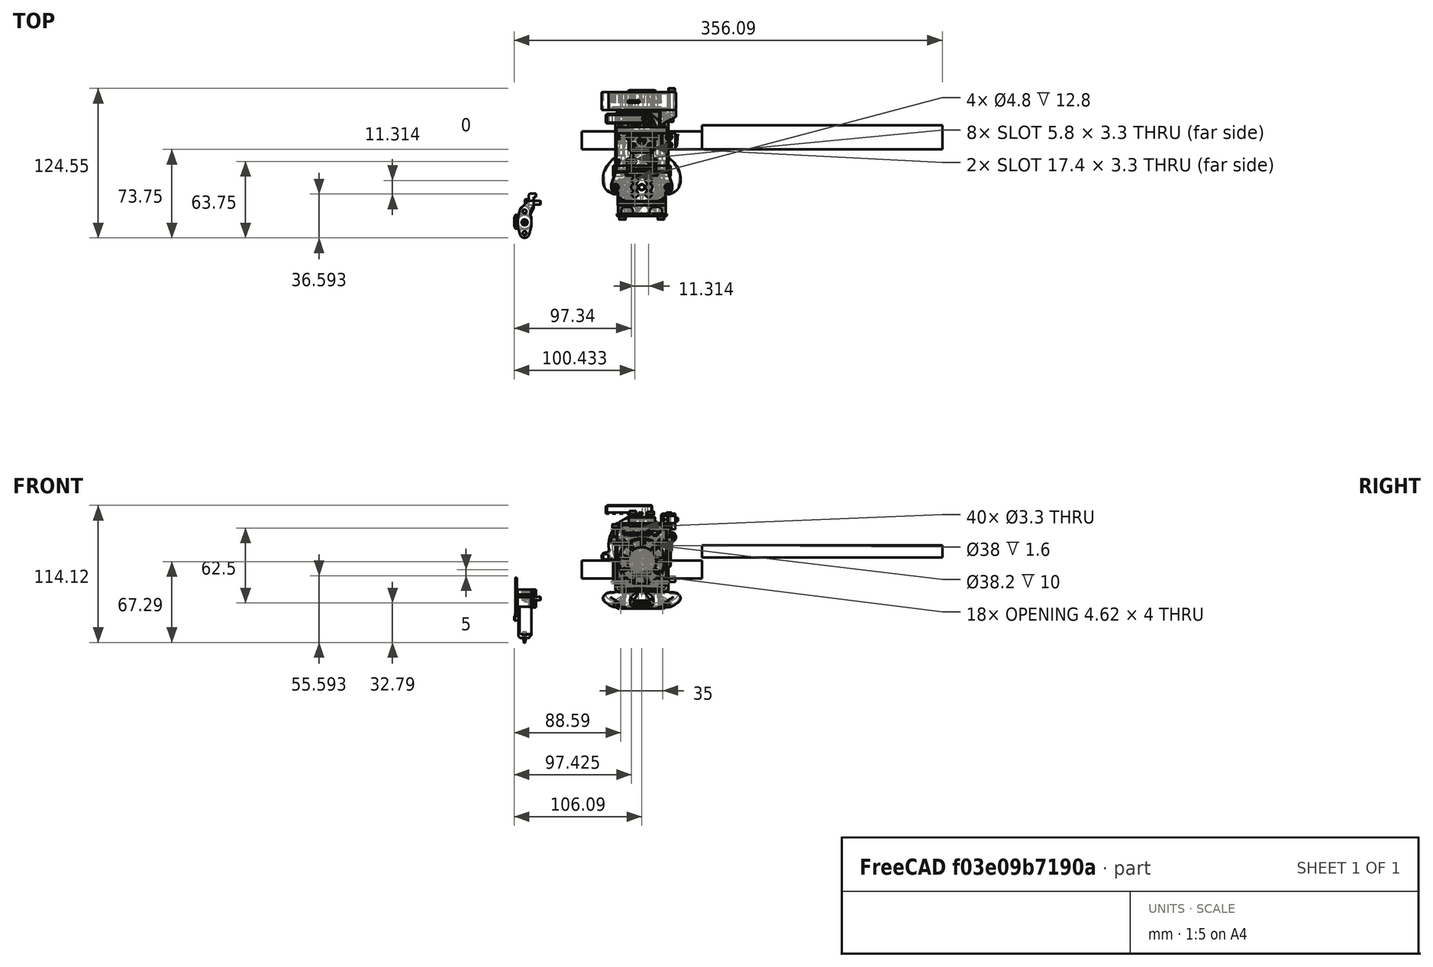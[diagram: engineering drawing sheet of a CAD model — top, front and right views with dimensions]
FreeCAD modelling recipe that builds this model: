
FCSTD DOCUMENT  (FreeCAD 0.19R24291 (Git))
Label: 2010-gantry
License: Other
LicenseURL: GPL3
objects: Part::Feature×106, Part::FeaturePython×104, App::Part×6, PartDesign::CoordinateSystem×2, Part::Box×2
note: 214 computed .brp shape members not serialized (recipe doc carries the construction recipe); baked Part::Feature solids carry a one-line shape summary decoded from their .brp

FEATURE [Part::FeaturePython] Screw1355  label="M3x40-Screw001"  # Fasteners workbench fastener (typed FeaturePython)
  Placement = pos=(-18.5,25.5,6) rot=(0,-1,0;1.5708rad)
  diameter = 4
  invert = false
  length = 10
  lengthCustom = 40
  matchOuter = true
  offset = 0
  thread = false
  type = 33
FEATURE [Part::FeaturePython] Screw1376  label="M2.5x12-Screw"  # Fasteners workbench fastener (typed FeaturePython)
  Placement = pos=(-6,-31.5,29.2) rot=(0,0,1;0rad)
  diameter = 3
  invert = false
  length = 10
  lengthCustom = 12
  matchOuter = true
  offset = 10
  thread = false
  type = 33
FEATURE [Part::Feature] Part__Feature112001140  label="adxl345 v009"
  shape: bbox 0.5 x 0.4946 x 0.1 mm, 6 faces (baked)
FEATURE [Part::FeaturePython] HeatSet014  label="M3x4-HeatSet010"  # WARN: FeaturePython — macro-defined, semantics opaque (R4)
  Placement = pos=(10.8,-13.5,27.705) rot=(-1,0,0;1.5708rad)
  diameter = 2
  invert = true
  offset = 0
FEATURE [Part::Feature] Part__Feature021  label="adxl345 v024"
  shape: bbox 0.5005 x 0.4962 x 0.1 mm, 6 faces (baked)
FEATURE [Part::Feature] Part__Feature013  label="adxl345 v016"
  shape: bbox 0.1939 x 0.3 x 0.1 mm, 6 faces (baked)
FEATURE [Part::Feature] Part__Feature112001127  label="adxl345 v017"
  shape: bbox 0.5 x 0.5 x 0.1 mm, 6 faces (baked)
FEATURE [Part::FeaturePython] Screw1381  label="M3x35-Screw"  # Fasteners workbench fastener (typed FeaturePython)
  Placement = pos=(17.0458,-16.5,41.0035) rot=(1,0,0;1.5708rad)
  diameter = 1
  invert = true
  length = 9
  lengthCustom = 35
  matchOuter = true
  offset = 0
  thread = false
  type = 39
FEATURE [Part::Feature] Part__Feature024  label="adxl345 v027"
  shape: bbox 0.5005 x 0.5054 x 0.15 mm, 6 faces (baked)
FEATURE [Part::FeaturePython] Nut  label="M3-Nut"  # Fasteners workbench fastener (typed FeaturePython)
  Placement = pos=(0,-15,-5.8) rot=(-1,0,0;1.5708rad)
  diameter = 4
  invert = true
  matchOuter = true
  offset = 0
  thread = false
  type = 7
FEATURE [Part::FeaturePython] Screw1371  label="M3x10-Screw189"  # Fasteners workbench fastener (typed FeaturePython)
  Placement = pos=(-94.0942,-44.3565,-16.7887) rot=(0,-1,0;1.5708rad)
  diameter = 4
  invert = false
  length = 10
  lengthCustom = 10
  matchOuter = true
  offset = 0
  thread = false
  type = 33
FEATURE [Part::FeaturePython] Screw020  label="M3x10-Screw"  # Fasteners workbench fastener (typed FeaturePython)
  Placement = pos=(-10.0042,-9.99647,39.1513) rot=(0,0,1;0rad)
  diameter = 4
  invert = false
  length = 10
  lengthCustom = 10
  matchOuter = true
  offset = 0
  thread = false
  type = 33
FEATURE [Part::FeaturePython] Nut005  label="M3-Nut030"  # Fasteners workbench fastener (typed FeaturePython)
  Placement = pos=(-13,15.5,-7) rot=(-1,0,0;1.5708rad)
  diameter = 4
  invert = false
  matchOuter = true
  offset = 0
  thread = false
  type = 7
FEATURE [Part::FeaturePython] HeatSet001  label="M3x4-HeatSet001"  # WARN: FeaturePython — macro-defined, semantics opaque (R4)
  Placement = pos=(-20,-36.5,11.7) rot=(0,-1,0;1.5708rad)
  baseObject = -> Chamfer005021077002006007019003029001 [Edge194]
  diameter = 2
  invert = false
  offset = 0
FEATURE [Part::FeaturePython] HeatSet019  label="M3x4-HeatSet017"  # WARN: FeaturePython — macro-defined, semantics opaque (R4)
  Placement = pos=(-21.9,-31.5,35) rot=(0,0,1;0rad)
  baseObject = -> Chamfer005021077002006007019003029001 [Edge1]
  diameter = 2
  invert = false
  offset = 0
FEATURE [Part::FeaturePython] Screw027  label="M3x25-Screw"  # Fasteners workbench fastener (typed FeaturePython)
  Placement = pos=(-10.8,-38.5,27.5) rot=(1,0,0;1.5708rad)
  diameter = 4
  invert = false
  length = 10
  lengthCustom = 25
  matchOuter = true
  offset = 0
  thread = false
  type = 33
FEATURE [Part::FeaturePython] HeatSet024  label="M3-HeatSet"  # WARN: FeaturePython — macro-defined, semantics opaque (R4)
  Placement = pos=(1.1e-14,13.5,42) rot=(-1,0,0;1.5708rad)
  baseObject = -> Chamfer005021077002006007019003032016001 [Edge74]
  diameter = 2
  invert = false
  offset = 0
FEATURE [Part::FeaturePython] Screw023  label="M3x12-Screw066"  # Fasteners workbench fastener (typed FeaturePython)
  Placement = pos=(21.9,-31.5,42) rot=(0,0,1;0rad)
  diameter = 4
  invert = false
  length = 10
  lengthCustom = 12
  matchOuter = true
  offset = 7
  thread = false
  type = 33
FEATURE [Part::FeaturePython] Screw1386  label="M3x12-Screw076"  # Fasteners workbench fastener (typed FeaturePython)
  Placement = pos=(0,25.5,42) rot=(-1,0,0;1.5708rad)
  baseObject = -> Chamfer001002006002 [Edge216]
  diameter = 4
  invert = true
  length = 4
  lengthCustom = 12
  matchOuter = true
  offset = 0
  thread = false
  type = 34
FEATURE [Part::FeaturePython] HeatSet006  label="M3x4-HeatSet007"  # WARN: FeaturePython — macro-defined, semantics opaque (R4)
  Placement = pos=(7.5,2.5,51) rot=(0,0,1;0rad)
  baseObject = -> Fusion036012039011002025018010027013001002002001002001029001 [Edge25]
  diameter = 2
  invert = false
  offset = 0
FEATURE [Part::Feature] Cut003  label="bl_touch_mount"
  Placement = pos=(-90,-44.75,-9.25) rot=(1,0,0;3.14159rad)
  shape: bbox 15.25 x 37 x 15 mm, 41 faces (baked)
FEATURE [Part::Feature] Part__Feature112001123  label="adxl345 v012"
  shape: bbox 0.5 x 0.5 x 0.1 mm, 6 faces (baked)
FEATURE [Part::FeaturePython] Screw1377  label="M2.5x12-Screw001"  # Fasteners workbench fastener (typed FeaturePython)
  Placement = pos=(6,-31.5,29.2) rot=(0,0,1;0rad)
  diameter = 3
  invert = false
  length = 10
  lengthCustom = 12
  matchOuter = true
  offset = 10
  thread = false
  type = 33
FEATURE [Part::FeaturePython] Screw018  label="M3x10-Screw186"  # Fasteners workbench fastener (typed FeaturePython)
  Placement = pos=(9.99577,-9.99647,39.1513) rot=(0,0,1;0rad)
  diameter = 4
  invert = true
  length = 10
  lengthCustom = 10
  matchOuter = true
  offset = 0
  thread = false
  type = 33
FEATURE [Part::Feature] Part__Feature020  label="adxl345 v023"
  shape: bbox 0.5 x 0.5 x 0.1 mm, 6 faces (baked)
FEATURE [Part::Feature] Part__Feature015  label="adxl345 v018"
  shape: bbox 0.5 x 0.5 x 0.1 mm, 6 faces (baked)
FEATURE [Part::Feature] Chamfer005021077002006007019003032007004003001001  label="1515-front-plate-r003"
  Placement = pos=(0,-13,10) rot=(1,0,0;1.5708rad)
  shape: bbox 48 x 9 x 57 mm, 252 faces (baked)
FEATURE [Part::FeaturePython] HeatSet015  label="M3x4-HeatSet012"  # WARN: FeaturePython — macro-defined, semantics opaque (R4)
  Placement = pos=(-10.8,-13.5,27.71) rot=(-1,0,0;1.5708rad)
  diameter = 2
  invert = true
  offset = 0
FEATURE [Part::Feature] Chamfer005021077002006007019003014001  label="face-plate"
  Placement = pos=(0,-56.5,-6) rot=(0,0,1;0rad)
  shape: bbox 41.5 x 7.5 x 53.5 mm, 789 faces (baked)
FEATURE [Part::FeaturePython] Screw1384  label="M3x12-Screw075"  # Fasteners workbench fastener (typed FeaturePython)
  Placement = pos=(17.5,18.5,-20.5) rot=(-1,0,0;1.5708rad)
  diameter = 4
  invert = false
  length = 4
  lengthCustom = 12
  matchOuter = true
  offset = 0
  thread = false
  type = 34
FEATURE [Part::Feature] Part__Feature112001136  label="5015 fan"
  Placement = pos=(-4.23967,32.8,25.9455) rot=(0.15487,0.698575,0.698575;3.44889rad)
  shape: bbox 61.97 x 15 x 62.93 mm, 220 faces (baked)
FEATURE [Part::FeaturePython] Screw1368  label="M3x25-Screw027"  # Fasteners workbench fastener (typed FeaturePython)
  Placement = pos=(24.8765,47.8,34.436) rot=(-1,0,0;1.5708rad)
  baseObject = -> Part__Feature112001136 [Edge8]
  diameter = 4
  invert = false
  length = 10
  lengthCustom = 25
  matchOuter = true
  offset = 0
  thread = false
  type = 33
FEATURE [Part::Feature] Part__Feature025  label="adxl345 v028"
  shape: bbox 0.5 x 0.5 x 0.15 mm, 6 faces (baked)
FEATURE [Part::Feature] Part__Feature112001130  label="adxl345 v034"
  shape: bbox 2 x 1 x 0.3 mm, 6 faces (baked)
FEATURE [Part::Feature] Part__Feature010  label="adxl345 v013"
  shape: bbox 0.5 x 0.4946 x 0.1 mm, 6 faces (baked)
FEATURE [Part::FeaturePython] Nut006  label="M3-Nut031"  # Fasteners workbench fastener (typed FeaturePython)
  Placement = pos=(24.8758,29.75,34.3023) rot=(1,0,0;1.5708rad)
  diameter = 4
  invert = false
  matchOuter = true
  offset = 0
  thread = false
  type = 7
FEATURE [Part::FeaturePython] Screw1385  label="M3x12-Screw074"  # Fasteners workbench fastener (typed FeaturePython)
  Placement = pos=(-17.5,18.5,-20.5) rot=(-1,0,0;1.5708rad)
  diameter = 4
  invert = true
  length = 4
  lengthCustom = 12
  matchOuter = true
  offset = 0
  thread = false
  type = 34
FEATURE [Part::Feature] Chamfer005021077002006007019003032007001  label="mosquito-mount-mod"
  Placement = pos=(0,-31.5,33) rot=(0,0,1;0rad)
  shape: bbox 51.01 x 27.77 x 40.81 mm, 154 faces (baked)
FEATURE [Part::FeaturePython] Screw1360  label="M3x35-Screw003"  # Fasteners workbench fastener (typed FeaturePython)
  Placement = pos=(12.9958,-16,-6.99647) rot=(1,0,0;1.5708rad)
  diameter = 4
  invert = true
  length = 10
  lengthCustom = 35
  matchOuter = true
  offset = 0
  thread = false
  type = 33
FEATURE [Part::FeaturePython] HeatSet017  label="M3x4-HeatSet013"  # WARN: FeaturePython — macro-defined, semantics opaque (R4)
  Placement = pos=(-10,25.5,19) rot=(0,-1,0;1.5708rad)
  baseObject = -> Chamfer005021077002006007019003032007003 [Edge5]
  diameter = 2
  invert = false
  offset = 0
FEATURE [Part::FeaturePython] Screw019  label="M3x10-Screw187"  # Fasteners workbench fastener (typed FeaturePython)
  Placement = pos=(-10.0042,10.0035,39.1513) rot=(0,0,1;0rad)
  diameter = 4
  invert = false
  length = 10
  lengthCustom = 10
  matchOuter = true
  offset = 0
  thread = false
  type = 33
FEATURE [Part::FeaturePython] HeatSet016  label="M3x4-HeatSet004"  # WARN: FeaturePython — macro-defined, semantics opaque (R4)
  Placement = pos=(10,25.5,6) rot=(0,1,0;1.5708rad)
  baseObject = -> Chamfer008009001 [Edge5]
  diameter = 2
  invert = false
  offset = 0
FEATURE [Part::Feature] Chamfer008009001  label="extruder-belt-tesioner"
  Placement = pos=(6,15,10) rot=(0,1,0;3.14159rad)
  shape: bbox 20 x 14.4 x 10 mm, 116 faces (baked)
FEATURE [Part::Feature] Part__Feature018  label="adxl345 v021"
  shape: bbox 0.5 x 2 x 0.1 mm, 6 faces (baked)
FEATURE [Part::FeaturePython] HeatSet018  label="M3x4-HeatSet018"  # WARN: FeaturePython — macro-defined, semantics opaque (R4)
  Placement = pos=(21.9,-31.5,35) rot=(0,0,1;0rad)
  baseObject = -> Chamfer005021077002006007019003029001 [Edge25]
  diameter = 2
  invert = false
  offset = 0
FEATURE [Part::Feature] Part__Feature028  label="adxl345 v031"
  shape: bbox 0.5 x 0.5054 x 0.15 mm, 6 faces (baked)
FEATURE [Part::Feature] Part__Feature005  label="adxl345 v008"
  shape: bbox 0.5 x 0.5 x 0.1 mm, 6 faces (baked)
FEATURE [Part::Feature] Fusion006002011004053036004001028003005014029  label="endstop-switch"
  Placement = pos=(28,7,46) rot=(0,0,1;1.5708rad)
  shape: bbox 12.18 x 13 x 6 mm, 43 faces (baked)
FEATURE [PartDesign::CoordinateSystem] LCS_toolhead_1515  label="LCS_toolhead-1515"
  AttacherType = Attacher::AttachEngine3D
FEATURE [Part::FeaturePython] Screw017  label="M3x10-Screw188"  # Fasteners workbench fastener (typed FeaturePython)
  Placement = pos=(9.99577,10.0035,39.1513) rot=(0,0,1;0rad)
  diameter = 4
  invert = true
  length = 10
  lengthCustom = 10
  matchOuter = true
  offset = 0
  thread = false
  type = 33
FEATURE [Part::Feature] Part__Feature112001141  label="adxl345 v011"
  shape: bbox 0.5 x 2 x 0.1 mm, 6 faces (baked)
FEATURE [Part::FeaturePython] Nut058  label="M3-Nut027"  # Fasteners workbench fastener (typed FeaturePython)
  Placement = pos=(17.05,15.5,41) rot=(-1,0,0;1.5708rad)
  diameter = 4
  invert = false
  matchOuter = true
  offset = 0
  thread = false
  type = 7
FEATURE [Part::Feature] Chamfer005021077002006007019003032007003  label="extruder-belt-tesioner001"
  Placement = pos=(-6,15,15) rot=(0,0,1;0rad)
  shape: bbox 20 x 14.4 x 10 mm, 116 faces (baked)
FEATURE [Part::Feature] Chamfer005021077002006007019003032016001  label="extruder-back-plate"
  Placement = pos=(1e-15,10,10) rot=(0,0.707107,0.707107;3.14159rad)
  shape: bbox 51.76 x 37.05 x 72.2 mm, 524 faces (baked)
FEATURE [Part::FeaturePython] Screw022  label="M3x12-Screw"  # Fasteners workbench fastener (typed FeaturePython)
  Placement = pos=(-21.9,-31.5,42) rot=(0,0,1;0rad)
  diameter = 4
  invert = false
  length = 10
  lengthCustom = 12
  matchOuter = true
  offset = 7
  thread = false
  type = 33
FEATURE [Part::Feature] Part__Feature029  label="adxl345 v032"
  shape: bbox 0.5 x 0.5054 x 0.15 mm, 6 faces (baked)
FEATURE [Part::Feature] Part__Feature026  label="adxl345 v029"
  shape: bbox 0.5 x 0.5054 x 0.15 mm, 6 faces (baked)
FEATURE [Part::Feature] Part__Feature011  label="adxl345 v014"
  shape: bbox 0.5 x 0.5 x 0.1 mm, 6 faces (baked)
FEATURE [Part::Feature] Part__Feature019  label="adxl345 v022"
  shape: bbox 0.5 x 0.4946 x 0.1 mm, 6 faces (baked)
FEATURE [Part::FeaturePython] Nut060  label="M3-Nut033"  # Fasteners workbench fastener (typed FeaturePython)
  Placement = pos=(17.5,8.59783,-20.5) rot=(1,0,0;1.5708rad)
  baseObject = -> Part__Feature003 [Edge202]
  diameter = 4
  invert = true
  matchOuter = true
  offset = 0
  thread = false
  type = 7
FEATURE [Part::FeaturePython] HeatSet004  label="M3x4-HeatSet009"  # WARN: FeaturePython — macro-defined, semantics opaque (R4)
  Placement = pos=(1e-14,7.5,46) rot=(0,0,1;0rad)
  baseObject = -> Body001002001 [Edge282]
  diameter = 2
  invert = true
  offset = 0
FEATURE [Part::FeaturePython] Screw1369  label="M3x25-Screw030"  # Fasteners workbench fastener (typed FeaturePython)
  Placement = pos=(10.8,-38.5,27.5) rot=(1,0,0;1.5708rad)
  diameter = 4
  invert = false
  length = 10
  lengthCustom = 25
  matchOuter = true
  offset = 0
  thread = false
  type = 33
FEATURE [Part::Feature] Part__Feature027  label="adxl345 v030"
  shape: bbox 0.5 x 0.5 x 0.15 mm, 6 faces (baked)
FEATURE [Part::Feature] Part__Feature112001139  label="BL-touch v3.x002"
  Placement = pos=(-97.5942,-60.3565,-13.2887) rot=(0,0,1;1.5708rad)
  shape: bbox 16.53 x 26.01 x 53.81 mm, 111 faces (baked)
FEATURE [App::Part] BL_Touch__1_001  label="BL-Touch <1>001"
  Group = -> [Part__Feature112001139,Screw1371,Cut003]
  Origin = -> Origin206
  Placement = pos=(70,8,28.5) rot=(0,0,1;0rad)
FEATURE [Part::FeaturePython] Screw1359  label="M3x35-Screw004"  # Fasteners workbench fastener (typed FeaturePython)
  Placement = pos=(-13.0042,-16,-6.99647) rot=(1,0,0;1.5708rad)
  diameter = 4
  invert = true
  length = 10
  lengthCustom = 35
  matchOuter = true
  offset = 0
  thread = false
  type = 33
FEATURE [Part::Feature] Part__Feature112001124  label="adxl345 v010"
  shape: bbox 0.5 x 0.5 x 0.1 mm, 6 faces (baked)
FEATURE [Part::Feature] Part__Feature112001143  label="dragon_support"
  Placement = pos=(-1.3e-14,-65.5,-44.5) rot=(1,0,0;3.14159rad)
  shape: bbox 40 x 20.25 x 9.266 mm, 50 faces (baked)
FEATURE [Part::FeaturePython] Screw1380  label="M3x35-Screw005"  # Fasteners workbench fastener (typed FeaturePython)
  Placement = pos=(-17.0542,-16.5,41.0035) rot=(1,0,0;1.5708rad)
  diameter = 1
  invert = true
  length = 9
  lengthCustom = 35
  matchOuter = true
  offset = 0
  thread = false
  type = 39
FEATURE [Part::Feature] Part__Feature112001133  label="mosquito_support"
  Placement = pos=(-2.78e-14,-21.6,27.5) rot=(0,0,1;0rad)
  shape: bbox 40 x 20.25 x 12 mm, 97 faces (baked)
FEATURE [Part::FeaturePython] Screw026  label="M3x8-Screw128"  # Fasteners workbench fastener (typed FeaturePython)
  Placement = pos=(3e-15,-20.15,-6) rot=(1,0,0;1.5708rad)
  baseObject = -> Part__Feature112001133 [Edge213]
  diameter = 4
  invert = true
  length = 10
  lengthCustom = 8
  matchOuter = true
  offset = 0
  thread = false
  type = 33
FEATURE [Part::Feature] Body001001001  label="endstop-cap"
  Placement = pos=(16,7,54) rot=(1,0,0;3.14159rad)
  shape: bbox 12 x 13 x 7.75 mm, 19 faces (baked)
FEATURE [Part::FeaturePython] Screw1383  label="M2x10-self-tapping"  # Fasteners workbench fastener (typed FeaturePython)
  Placement = pos=(22.75,10.25,53) rot=(0,0,1;0rad)
  baseObject = -> Body001001001 [Edge25]
  diameter = 2
  invert = false
  length = 5
  lengthCustom = 10
  matchOuter = true
  offset = 0
  thread = false
  type = 33
FEATURE [Part::FeaturePython] Screw1382  label="M2x10-self-tapping001"  # Fasteners workbench fastener (typed FeaturePython)
  Placement = pos=(22.75,3.75,53) rot=(0,0,1;0rad)
  baseObject = -> Body001001001 [Edge27]
  diameter = 2
  invert = false
  length = 5
  lengthCustom = 10
  matchOuter = true
  offset = 0
  thread = false
  type = 33
FEATURE [Part::FeaturePython] Screw1356  label="M3x40-Screw"  # Fasteners workbench fastener (typed FeaturePython)
  Placement = pos=(18.5,25.5,19) rot=(0,1,0;1.5708rad)
  diameter = 4
  invert = false
  length = 10
  lengthCustom = 40
  matchOuter = true
  offset = 0
  thread = false
  type = 33
FEATURE [Part::FeaturePython] HeatSet002  label="M3x4-HeatSet003"  # WARN: FeaturePython — macro-defined, semantics opaque (R4)
  Placement = pos=(20,-36.5,11.7) rot=(0,1,0;1.5708rad)
  baseObject = -> Chamfer005021077002006007019003029001 [Edge128]
  diameter = 2
  invert = true
  offset = 0
FEATURE [Part::Feature] Body001002001  label="top-plate-with-endstop"
  Placement = pos=(0,0,0) rot=(0,0,1;3.14159rad)
  shape: bbox 50.05 x 27 x 13 mm, 100 faces (baked)
FEATURE [Part::FeaturePython] Nut059  label="M3-Nut032"  # Fasteners workbench fastener (typed FeaturePython)
  Placement = pos=(-17.5,8.59783,-20.5) rot=(1,0,0;1.5708rad)
  baseObject = -> Part__Feature003 [Edge75]
  diameter = 4
  invert = false
  matchOuter = true
  offset = 0
  thread = false
  type = 7
FEATURE [Part::Feature] Fusion006002011004053036004001028003005014018035002010  label="mosquito-hotend"
  Placement = pos=(0,-31.5,-28) rot=(0,0,1;0rad)
  shape: bbox 27.01 x 18.86 x 47.01 mm, 355 faces, 0 solids (baked)
FEATURE [Part::FeaturePython] Nut004  label="M3-Nut009"  # Fasteners workbench fastener (typed FeaturePython)
  Placement = pos=(13,15.5,-7) rot=(-1,0,0;1.5708rad)
  diameter = 4
  invert = false
  matchOuter = true
  offset = 0
  thread = false
  type = 7
FEATURE [Part::Feature] Chamfer001002006002  label="extruder-cable-support"
  Placement = pos=(0,29.5,32) rot=(1,0,0;1.5708rad)
  shape: bbox 38.86 x 11.83 x 29.43 mm, 90 faces (baked)
FEATURE [Part::FeaturePython] HeatSet005  label="M3x4-HeatSet008"  # WARN: FeaturePython — macro-defined, semantics opaque (R4)
  Placement = pos=(-7.5,2.5,51) rot=(0,0,1;0rad)
  baseObject = -> Fusion036012039011002025018010027013001002002001002001029001 [Edge5]
  diameter = 2
  invert = false
  offset = 0
FEATURE [Part::Feature] Part__Feature006  label="extruderbottom-plate"
  Placement = pos=(0,17.6378,-29.79) rot=(1,0,0;1.5708rad)
  shape: bbox 44.1 x 27 x 22.2 mm, 66 faces (baked)
FEATURE [Part::Feature] Part__Feature004  label="adxl345 v007"
  shape: bbox 0.5 x 0.5 x 0.1 mm, 6 faces (baked)
FEATURE [Part::Feature] Part__Feature016  label="adxl345 v019"
  shape: bbox 0.5 x 0.5 x 0.1 mm, 6 faces (baked)
FEATURE [Part::FeaturePython] HeatSet003  label="M3x4-HeatSet"  # WARN: FeaturePython — macro-defined, semantics opaque (R4)
  Placement = pos=(20,-36.5,3.7) rot=(0,1,0;1.5708rad)
  baseObject = -> Chamfer005021077002006007019003029001 [Edge127]
  diameter = 2
  invert = true
  offset = 0
FEATURE [Part::Feature] Part__Feature112001126  label="adxl345 v005"
  shape: bbox 4 x 2 x 1 mm, 6 faces (baked)
FEATURE [Part::Feature] Part__Feature023  label="adxl345 v026"
  shape: bbox 0.1911 x 0.3 x 0.1 mm, 6 faces (baked)
FEATURE [Part::Feature] Chamfer005021077002006007019003029001  label="dragon-mount-mod"
  Placement = pos=(0,-31.5,33) rot=(0,0,1;0rad)
  shape: bbox 51.01 x 26.2 x 43.01 mm, 143 faces (baked)
FEATURE [Part::Feature] Part__Feature112001125  label="adxl345 v006"
  shape: bbox 0.2125 x 0.3 x 0.1 mm, 6 faces (baked)
FEATURE [Part::Feature] Part__Feature012  label="adxl345 v015"
  shape: bbox 0.2125 x 0.4 x 0.1 mm, 6 faces (baked)
FEATURE [Part::FeaturePython] Nut057  label="M3-Nut026"  # Fasteners workbench fastener (typed FeaturePython)
  Placement = pos=(-17.05,15.5,41) rot=(-1,0,0;1.5708rad)
  diameter = 4
  invert = false
  matchOuter = true
  offset = 0
  thread = false
  type = 7
FEATURE [Part::Feature] Part__Feature030  label="adxl345 v033"
  shape: bbox 0.5 x 0.5 x 0.15 mm, 6 faces (baked)
FEATURE [Part::Feature] Part__Feature112001131  label="4010-fan"
  Placement = pos=(-2.4e-14,-43.5,14) rot=(0,0,1;0rad)
  shape: bbox 40 x 10 x 40 mm, 104 faces (baked)
FEATURE [Part::FeaturePython] Screw1375  label="M3x25-Screw029"  # Fasteners workbench fastener (typed FeaturePython)
  Placement = pos=(16,-55.5,-2) rot=(1,0,0;1.5708rad)
  baseObject = -> Part__Feature112001131 [Edge121]
  diameter = 4
  invert = false
  length = 10
  lengthCustom = 25
  matchOuter = true
  offset = 2
  thread = false
  type = 33
FEATURE [Part::FeaturePython] Screw1374  label="M3x25-Screw004"  # Fasteners workbench fastener (typed FeaturePython)
  Placement = pos=(-16,-55.5,-2) rot=(1,0,0;1.5708rad)
  baseObject = -> Part__Feature112001131 [Edge127]
  diameter = 4
  invert = false
  length = 10
  lengthCustom = 25
  matchOuter = true
  offset = 2
  thread = false
  type = 33
FEATURE [Part::FeaturePython] Screw1372  label="M3x20-Screw023"  # Fasteners workbench fastener (typed FeaturePython)
  Placement = pos=(-16,-55.5,30) rot=(1,0,0;1.5708rad)
  baseObject = -> Part__Feature112001131 [Edge130]
  diameter = 4
  invert = false
  length = 10
  lengthCustom = 20
  matchOuter = true
  offset = 2
  thread = false
  type = 33
FEATURE [Part::FeaturePython] Screw1373  label="M3x20-Screw024"  # Fasteners workbench fastener (typed FeaturePython)
  Placement = pos=(16,-55.5,30) rot=(1,0,0;1.5708rad)
  baseObject = -> Part__Feature112001131 [Edge124]
  diameter = 4
  invert = false
  length = 10
  lengthCustom = 20
  matchOuter = true
  offset = 2
  thread = false
  type = 33
FEATURE [Part::Feature] Part__Feature017  label="adxl345 v020"
  shape: bbox 0.5 x 0.5 x 0.1 mm, 6 faces (baked)
FEATURE [Part::Feature] Part__Feature022  label="adxl345 v025"
  shape: bbox 0.1911 x 0.4 x 0.1 mm, 6 faces (baked)
FEATURE [Part::Feature] Part__Feature003  label="duct-tri-horn"
  Placement = pos=(0,10.5978,-18) rot=(1,0,0;1.5708rad)
  shape: bbox 65.34 x 50.74 x 15.61 mm, 106 faces (baked)
FEATURE [Part::FeaturePython] Screw  label="M3x8-Screw"  # Fasteners workbench fastener (typed FeaturePython)
  Placement = pos=(0,7.5,48.5) rot=(0,0,1;0rad)
  diameter = 1
  invert = false
  length = 1
  lengthCustom = 8
  matchOuter = true
  offset = 0
  thread = false
  type = 39
FEATURE [Part::Feature] Fusion036012039011002025018010027013001002002001002001029001  label="adxl-mount"
  Placement = pos=(0,-31.5,33) rot=(0,0,1;0rad)
  shape: bbox 22 x 12.5 x 6.5 mm, 26 faces (baked)
FEATURE [Part::FeaturePython] Screw1378  label="M3x6-Screw"  # Fasteners workbench fastener (typed FeaturePython)
  Placement = pos=(-7.5,2.5,53) rot=(0,0,1;0rad)
  baseObject = -> Fusion036012039011002025018010027013001002002001002001029001 [Edge2]
  diameter = 4
  invert = false
  length = 1
  lengthCustom = 6
  matchOuter = true
  offset = 2.4
  thread = false
  type = 33
FEATURE [Part::FeaturePython] Screw1379  label="M3x6-Screw105"  # Fasteners workbench fastener (typed FeaturePython)
  Placement = pos=(7.5,2.5,52.6) rot=(0,0,1;0rad)
  baseObject = -> Fusion036012039011002025018010027013001002002001002001029001 [Edge47]
  diameter = 4
  invert = false
  length = 1
  lengthCustom = 6
  matchOuter = true
  offset = 2
  thread = false
  type = 33
FEATURE [Part::Feature] Part__Feature112001129  label="adxl345 v3"
  shape: bbox 6 x 3 x 0.5 mm, 6 faces (baked)
FEATURE [Part::Feature] Part__Feature112001128  label="adxl345 v004"
  shape: bbox 20 x 15 x 1.27 mm, 8 faces (baked)
FEATURE [App::Part] adxl345_v3  label="adxl345"
  Group = -> [Part__Feature112001129,Part__Feature112001128,Part__Feature112001126,Part__Feature112001125,Part__Feature004,Part__Feature005,Part__Feature112001140,Part__Feature112001124,Part__Feature112001141,Part__Feature112001123,Part__Feature010,Part__Feature011,Part__Feature012,Part__Feature013,Part__Feature112001127,Part__Feature015,Part__Feature016,Part__Feature017,Part__Feature018,Part__Feature019,+12 more]
  Origin = -> Origin004
  Placement = pos=(-10,0.5,52.5) rot=(0,0,1;0rad)
FEATURE [App::Part] Part197  label="toolhead-carrier-sherpa-1515"
  Group = -> [Fusion006002011004053036004001028003005014018035002010,Part__Feature112001133,Part__Feature112001136,Part__Feature112001131,BL_Touch__1_001,Nut006,Nut058,Nut005,Nut004,Screw1355,Screw1356,Nut057,Screw1360,Screw1359,Screw1368,Screw022,Screw018,Screw020,Screw023,Screw019,Screw017,Screw026,Screw1376,Screw1377,Screw1369,Screw027,Screw1373,Screw1375,Screw1374,Screw1372,adxl345_v3,+42 more]
  Origin = -> Origin205
  Placement = pos=(0,7.5,-5) rot=(0,0,1;0rad)
FEATURE [Part::Box] Box  label="Cube"
  AttacherType = Attacher::AttachEngine3D
  Height = 15
  Length = 100
  Placement = pos=(-50,0,0) rot=(0,0,1;0rad)
  Width = 15
FEATURE [Part::Box] Box001  label="Cube001"
  AttacherType = Attacher::AttachEngine3D
  Height = 10
  Length = 200
  Placement = pos=(50,0,17.5) rot=(0,0,1;0rad)
  Width = 20
FEATURE [Part::FeaturePython] Screw1387  label="M3x40-Screw002"  # Fasteners workbench fastener (typed FeaturePython)
  Placement = pos=(-18.5,25.5,6) rot=(0,-1,0;1.5708rad)
  diameter = 4
  invert = false
  length = 10
  lengthCustom = 40
  matchOuter = true
  offset = 0
  thread = false
  type = 33
FEATURE [Part::Feature] Part__Feature112001144  label="adxl345 v035"
  shape: bbox 0.5 x 2 x 0.1 mm, 6 faces (baked)
FEATURE [Part::FeaturePython] Screw1388  label="M2.5x12-Screw002"  # Fasteners workbench fastener (typed FeaturePython)
  Placement = pos=(-6,-31.5,29.2) rot=(0,0,1;0rad)
  diameter = 3
  invert = false
  length = 10
  lengthCustom = 12
  matchOuter = true
  offset = 10
  thread = false
  type = 33
FEATURE [Part::Feature] Part__Feature112001145  label="adxl345 v036"
  shape: bbox 0.5 x 0.4946 x 0.1 mm, 6 faces (baked)
FEATURE [Part::FeaturePython] HeatSet025  label="M3x4-HeatSet019"  # WARN: FeaturePython — macro-defined, semantics opaque (R4)
  Placement = pos=(10.8,-13.5,27.705) rot=(-1,0,0;1.5708rad)
  diameter = 2
  invert = true
  offset = 0
FEATURE [Part::Feature] Part__Feature112001146  label="adxl345 v037"
  shape: bbox 0.5005 x 0.4962 x 0.1 mm, 6 faces (baked)
FEATURE [Part::Feature] Part__Feature112001147  label="adxl345 v038"
  shape: bbox 0.1939 x 0.3 x 0.1 mm, 6 faces (baked)
FEATURE [Part::Feature] Part__Feature112001148  label="adxl345 v039"
  shape: bbox 0.5 x 0.5 x 0.1 mm, 6 faces (baked)
FEATURE [Part::FeaturePython] Screw1393  label="M3x35-Screw006"  # Fasteners workbench fastener (typed FeaturePython)
  Placement = pos=(17.0458,-16.5,41.0035) rot=(1,0,0;1.5708rad)
  diameter = 1
  invert = true
  length = 9
  lengthCustom = 35
  matchOuter = true
  offset = 0
  thread = false
  type = 39
FEATURE [Part::Feature] Part__Feature112001149  label="adxl345 v040"
  shape: bbox 0.5005 x 0.5054 x 0.15 mm, 6 faces (baked)
FEATURE [Part::FeaturePython] Nut061  label="M3-Nut034"  # Fasteners workbench fastener (typed FeaturePython)
  Placement = pos=(0,-15,-5.8) rot=(-1,0,0;1.5708rad)
  diameter = 4
  invert = true
  matchOuter = true
  offset = 0
  thread = false
  type = 7
FEATURE [Part::FeaturePython] Screw1394  label="M3x10-Screw190"  # Fasteners workbench fastener (typed FeaturePython)
  Placement = pos=(-94.0942,-44.3565,-16.7887) rot=(0,-1,0;1.5708rad)
  diameter = 4
  invert = false
  length = 10
  lengthCustom = 10
  matchOuter = true
  offset = 0
  thread = false
  type = 33
FEATURE [Part::FeaturePython] Screw1395  label="M3x10-Screw191"  # Fasteners workbench fastener (typed FeaturePython)
  Placement = pos=(-10.0042,-9.99647,39.1513) rot=(0,0,1;0rad)
  diameter = 4
  invert = false
  length = 10
  lengthCustom = 10
  matchOuter = true
  offset = 0
  thread = false
  type = 33
FEATURE [Part::FeaturePython] Nut062  label="M3-Nut035"  # Fasteners workbench fastener (typed FeaturePython)
  Placement = pos=(-13,15.5,-7) rot=(-1,0,0;1.5708rad)
  diameter = 4
  invert = false
  matchOuter = true
  offset = 0
  thread = false
  type = 7
FEATURE [Part::FeaturePython] HeatSet026  label="M3x4-HeatSet020"  # WARN: FeaturePython — macro-defined, semantics opaque (R4)
  Placement = pos=(-20,-36.5,11.7) rot=(0,-1,0;1.5708rad)
  baseObject = -> Chamfer005021077002006007019003032007004003001009 [Edge194]
  diameter = 2
  invert = false
  offset = 0
FEATURE [Part::FeaturePython] HeatSet027  label="M3x4-HeatSet021"  # WARN: FeaturePython — macro-defined, semantics opaque (R4)
  Placement = pos=(-21.9,-31.5,35) rot=(0,0,1;0rad)
  baseObject = -> Chamfer005021077002006007019003032007004003001009 [Edge1]
  diameter = 2
  invert = false
  offset = 0
FEATURE [Part::FeaturePython] Screw1396  label="M3x25-Screw033"  # Fasteners workbench fastener (typed FeaturePython)
  Placement = pos=(-10.8,-38.5,27.5) rot=(1,0,0;1.5708rad)
  diameter = 4
  invert = false
  length = 10
  lengthCustom = 25
  matchOuter = true
  offset = 0
  thread = false
  type = 33
FEATURE [Part::FeaturePython] HeatSet028  label="M3-HeatSet001"  # WARN: FeaturePython — macro-defined, semantics opaque (R4)
  Placement = pos=(1.1e-14,13.5,42) rot=(-1,0,0;1.5708rad)
  baseObject = -> Chamfer005021077002006007019003032007004003001007 [Edge74]
  diameter = 2
  invert = false
  offset = 0
FEATURE [Part::FeaturePython] Screw1397  label="M3x12-Screw077"  # Fasteners workbench fastener (typed FeaturePython)
  Placement = pos=(21.9,-31.5,42) rot=(0,0,1;0rad)
  diameter = 4
  invert = false
  length = 10
  lengthCustom = 12
  matchOuter = true
  offset = 7
  thread = false
  type = 33
FEATURE [Part::FeaturePython] Screw1399  label="M3x12-Screw078"  # Fasteners workbench fastener (typed FeaturePython)
  Placement = pos=(0,25.5,42) rot=(-1,0,0;1.5708rad)
  baseObject = -> Chamfer005021077002006007019003032007004003001008 [Edge216]
  diameter = 4
  invert = true
  length = 4
  lengthCustom = 12
  matchOuter = true
  offset = 0
  thread = false
  type = 34
FEATURE [Part::FeaturePython] HeatSet029  label="M3x4-HeatSet022"  # WARN: FeaturePython — macro-defined, semantics opaque (R4)
  Placement = pos=(7.5,2.5,51) rot=(0,0,1;0rad)
  baseObject = -> Fusion036012039011002025018010027013001002002001002001029004 [Edge25]
  diameter = 2
  invert = false
  offset = 0
FEATURE [Part::Feature] Cut004  label="bl_touch_mount001"
  Placement = pos=(-90,-44.75,-9.25) rot=(1,0,0;3.14159rad)
  shape: bbox 15.25 x 37 x 15 mm, 41 faces (baked)
FEATURE [Part::Feature] Part__Feature112001150  label="adxl345 v041"
  shape: bbox 0.5 x 0.5 x 0.1 mm, 6 faces (baked)
FEATURE [Part::FeaturePython] Screw1400  label="M2.5x12-Screw003"  # Fasteners workbench fastener (typed FeaturePython)
  Placement = pos=(6,-31.5,29.2) rot=(0,0,1;0rad)
  diameter = 3
  invert = false
  length = 10
  lengthCustom = 12
  matchOuter = true
  offset = 10
  thread = false
  type = 33
FEATURE [Part::FeaturePython] Screw1401  label="M3x10-Screw192"  # Fasteners workbench fastener (typed FeaturePython)
  Placement = pos=(9.99577,-9.99647,39.1513) rot=(0,0,1;0rad)
  diameter = 4
  invert = true
  length = 10
  lengthCustom = 10
  matchOuter = true
  offset = 0
  thread = false
  type = 33
FEATURE [Part::Feature] Part__Feature112001151  label="adxl345 v042"
  shape: bbox 0.5 x 0.5 x 0.1 mm, 6 faces (baked)
FEATURE [Part::Feature] Part__Feature112001152  label="adxl345 v043"
  shape: bbox 0.5 x 0.5 x 0.1 mm, 6 faces (baked)
FEATURE [Part::Feature] Chamfer005021077002006007019003032007004003001002  label="1515-front-plate-r004"
  Placement = pos=(0,-13,10) rot=(1,0,0;1.5708rad)
  shape: bbox 48 x 9 x 57 mm, 252 faces (baked)
FEATURE [Part::FeaturePython] HeatSet030  label="M3x4-HeatSet023"  # WARN: FeaturePython — macro-defined, semantics opaque (R4)
  Placement = pos=(-10.8,-13.5,27.71) rot=(-1,0,0;1.5708rad)
  diameter = 2
  invert = true
  offset = 0
FEATURE [Part::Feature] Chamfer005021077002006007019003032007004003001003  label="face-plate001"
  Placement = pos=(0,-56.5,-6) rot=(0,0,1;0rad)
  shape: bbox 41.5 x 7.5 x 53.5 mm, 789 faces (baked)
FEATURE [Part::FeaturePython] Screw1402  label="M3x12-Screw079"  # Fasteners workbench fastener (typed FeaturePython)
  Placement = pos=(17.5,18.5,-20.5) rot=(-1,0,0;1.5708rad)
  diameter = 4
  invert = false
  length = 4
  lengthCustom = 12
  matchOuter = true
  offset = 0
  thread = false
  type = 34
FEATURE [Part::Feature] Part__Feature112001153  label="5015 fan001"
  Placement = pos=(-4.23967,32.8,25.9455) rot=(0.15487,0.698575,0.698575;3.44889rad)
  shape: bbox 61.97 x 15 x 62.93 mm, 220 faces (baked)
FEATURE [Part::FeaturePython] Screw1398  label="M3x25-Screw034"  # Fasteners workbench fastener (typed FeaturePython)
  Placement = pos=(24.8765,47.8,34.436) rot=(-1,0,0;1.5708rad)
  baseObject = -> Part__Feature112001153 [Edge8]
  diameter = 4
  invert = false
  length = 10
  lengthCustom = 25
  matchOuter = true
  offset = 0
  thread = false
  type = 33
FEATURE [Part::Feature] Part__Feature112001154  label="adxl345 v044"
  shape: bbox 0.5 x 0.5 x 0.15 mm, 6 faces (baked)
FEATURE [Part::Feature] Part__Feature112001155  label="adxl345 v045"
  shape: bbox 2 x 1 x 0.3 mm, 6 faces (baked)
FEATURE [Part::Feature] Part__Feature112001156  label="adxl345 v046"
  shape: bbox 0.5 x 0.4946 x 0.1 mm, 6 faces (baked)
FEATURE [Part::FeaturePython] Nut063  label="M3-Nut036"  # Fasteners workbench fastener (typed FeaturePython)
  Placement = pos=(24.8758,29.75,34.3023) rot=(1,0,0;1.5708rad)
  diameter = 4
  invert = false
  matchOuter = true
  offset = 0
  thread = false
  type = 7
FEATURE [Part::FeaturePython] Screw1403  label="M3x12-Screw080"  # Fasteners workbench fastener (typed FeaturePython)
  Placement = pos=(-17.5,18.5,-20.5) rot=(-1,0,0;1.5708rad)
  diameter = 4
  invert = true
  length = 4
  lengthCustom = 12
  matchOuter = true
  offset = 0
  thread = false
  type = 34
FEATURE [Part::Feature] Chamfer005021077002006007019003032007004003001004  label="mosquito-mount-mod001"
  Placement = pos=(0,-31.5,33) rot=(0,0,1;0rad)
  shape: bbox 51.01 x 27.77 x 40.81 mm, 154 faces (baked)
FEATURE [Part::FeaturePython] Screw1404  label="M3x35-Screw007"  # Fasteners workbench fastener (typed FeaturePython)
  Placement = pos=(12.9958,-16,-6.99647) rot=(1,0,0;1.5708rad)
  diameter = 4
  invert = true
  length = 10
  lengthCustom = 35
  matchOuter = true
  offset = 0
  thread = false
  type = 33
FEATURE [Part::FeaturePython] HeatSet031  label="M3x4-HeatSet024"  # WARN: FeaturePython — macro-defined, semantics opaque (R4)
  Placement = pos=(-10,25.5,19) rot=(0,-1,0;1.5708rad)
  baseObject = -> Chamfer005021077002006007019003032007004003001006 [Edge5]
  diameter = 2
  invert = false
  offset = 0
FEATURE [Part::FeaturePython] Screw1406  label="M3x10-Screw193"  # Fasteners workbench fastener (typed FeaturePython)
  Placement = pos=(-10.0042,10.0035,39.1513) rot=(0,0,1;0rad)
  diameter = 4
  invert = false
  length = 10
  lengthCustom = 10
  matchOuter = true
  offset = 0
  thread = false
  type = 33
FEATURE [Part::FeaturePython] HeatSet032  label="M3x4-HeatSet025"  # WARN: FeaturePython — macro-defined, semantics opaque (R4)
  Placement = pos=(10,25.5,6) rot=(0,1,0;1.5708rad)
  baseObject = -> Chamfer005021077002006007019003032007004003001005 [Edge5]
  diameter = 2
  invert = false
  offset = 0
FEATURE [Part::Feature] Chamfer005021077002006007019003032007004003001005  label="extruder-belt-tesioner002"
  Placement = pos=(6,15,10) rot=(0,1,0;3.14159rad)
  shape: bbox 20 x 14.4 x 10 mm, 116 faces (baked)
FEATURE [Part::Feature] Part__Feature112001157  label="adxl345 v047"
  shape: bbox 0.5 x 2 x 0.1 mm, 6 faces (baked)
FEATURE [Part::FeaturePython] HeatSet033  label="M3x4-HeatSet026"  # WARN: FeaturePython — macro-defined, semantics opaque (R4)
  Placement = pos=(21.9,-31.5,35) rot=(0,0,1;0rad)
  baseObject = -> Chamfer005021077002006007019003032007004003001009 [Edge25]
  diameter = 2
  invert = false
  offset = 0
FEATURE [Part::Feature] Part__Feature112001158  label="adxl345 v048"
  shape: bbox 0.5 x 0.5054 x 0.15 mm, 6 faces (baked)
FEATURE [Part::Feature] Part__Feature112001159  label="adxl345 v049"
  shape: bbox 0.5 x 0.5 x 0.1 mm, 6 faces (baked)
FEATURE [Part::Feature] Part__Feature112001160  label="adxl345 v050"
  shape: bbox 20 x 15 x 1.27 mm, 8 faces (baked)
FEATURE [Part::Feature] Fusion036012039011002025018010027013001002002001002001029002  label="endstop-switch001"
  Placement = pos=(28,7,46) rot=(0,0,1;1.5708rad)
  shape: bbox 12.18 x 13 x 6 mm, 43 faces (baked)
FEATURE [PartDesign::CoordinateSystem] LCS_toolhead_1516  label="LCS_toolhead-1516"
  AttacherType = Attacher::AttachEngine3D
FEATURE [Part::FeaturePython] Screw1408  label="M3x10-Screw194"  # Fasteners workbench fastener (typed FeaturePython)
  Placement = pos=(9.99577,10.0035,39.1513) rot=(0,0,1;0rad)
  diameter = 4
  invert = true
  length = 10
  lengthCustom = 10
  matchOuter = true
  offset = 0
  thread = false
  type = 33
FEATURE [Part::FeaturePython] Nut064  label="M3-Nut037"  # Fasteners workbench fastener (typed FeaturePython)
  Placement = pos=(17.05,15.5,41) rot=(-1,0,0;1.5708rad)
  diameter = 4
  invert = false
  matchOuter = true
  offset = 0
  thread = false
  type = 7
FEATURE [Part::Feature] Chamfer005021077002006007019003032007004003001006  label="extruder-belt-tesioner003"
  Placement = pos=(-6,15,15) rot=(0,0,1;0rad)
  shape: bbox 20 x 14.4 x 10 mm, 116 faces (baked)
FEATURE [Part::Feature] Chamfer005021077002006007019003032007004003001007  label="extruder-back-plate001"
  Placement = pos=(1e-15,10,10) rot=(0,0.707107,0.707107;3.14159rad)
  shape: bbox 51.76 x 37.05 x 72.2 mm, 524 faces (baked)
FEATURE [Part::FeaturePython] Screw1409  label="M3x12-Screw081"  # Fasteners workbench fastener (typed FeaturePython)
  Placement = pos=(-21.9,-31.5,42) rot=(0,0,1;0rad)
  diameter = 4
  invert = false
  length = 10
  lengthCustom = 12
  matchOuter = true
  offset = 7
  thread = false
  type = 33
FEATURE [Part::Feature] Part__Feature112001161  label="adxl345 v051"
  shape: bbox 0.5 x 0.5054 x 0.15 mm, 6 faces (baked)
FEATURE [Part::Feature] Part__Feature112001162  label="adxl345 v052"
  shape: bbox 0.5 x 0.5054 x 0.15 mm, 6 faces (baked)
FEATURE [Part::Feature] Part__Feature112001163  label="adxl345 v053"
  shape: bbox 0.5 x 0.5 x 0.1 mm, 6 faces (baked)
FEATURE [Part::Feature] Part__Feature112001164  label="adxl345 v054"
  shape: bbox 0.5 x 0.4946 x 0.1 mm, 6 faces (baked)
FEATURE [Part::FeaturePython] Nut065  label="M3-Nut038"  # Fasteners workbench fastener (typed FeaturePython)
  Placement = pos=(17.5,8.59783,-20.5) rot=(1,0,0;1.5708rad)
  baseObject = -> Part__Feature112001181 [Edge202]
  diameter = 4
  invert = true
  matchOuter = true
  offset = 0
  thread = false
  type = 7
FEATURE [Part::FeaturePython] HeatSet034  label="M3x4-HeatSet027"  # WARN: FeaturePython — macro-defined, semantics opaque (R4)
  Placement = pos=(1.03e-14,7.5,2) rot=(0,0,1;0rad)
  baseObject = -> Body001002003 [Edge282]
  diameter = 2
  invert = true
  offset = 0
FEATURE [Part::FeaturePython] Screw1411  label="M3x25-Screw035"  # Fasteners workbench fastener (typed FeaturePython)
  Placement = pos=(10.8,-38.5,27.5) rot=(1,0,0;1.5708rad)
  diameter = 4
  invert = false
  length = 10
  lengthCustom = 25
  matchOuter = true
  offset = 0
  thread = false
  type = 33
FEATURE [Part::Feature] Part__Feature112001165  label="adxl345 v055"
  shape: bbox 0.5 x 0.5 x 0.15 mm, 6 faces (baked)
FEATURE [Part::Feature] Part__Feature112001166  label="BL-touch v3.x003"
  Placement = pos=(-97.5942,-60.3565,-13.2887) rot=(0,0,1;1.5708rad)
  shape: bbox 16.53 x 26.01 x 53.81 mm, 111 faces (baked)
FEATURE [App::Part] BL_Touch__1_002  label="BL-Touch <1>002"
  Group = -> [Part__Feature112001166,Screw1394,Cut004]
  Origin = -> Origin208
  Placement = pos=(70,8,28.5) rot=(0,0,1;0rad)
FEATURE [Part::FeaturePython] Screw1412  label="M3x35-Screw008"  # Fasteners workbench fastener (typed FeaturePython)
  Placement = pos=(-13.0042,-16,-6.99647) rot=(1,0,0;1.5708rad)
  diameter = 4
  invert = true
  length = 10
  lengthCustom = 35
  matchOuter = true
  offset = 0
  thread = false
  type = 33
FEATURE [Part::Feature] Part__Feature112001167  label="adxl345 v056"
  shape: bbox 0.5 x 0.5 x 0.1 mm, 6 faces (baked)
FEATURE [Part::Feature] Part__Feature112001168  label="dragon_support001"
  Placement = pos=(-1.3e-14,-65.5,-44.5) rot=(1,0,0;3.14159rad)
  shape: bbox 40 x 20.25 x 9.266 mm, 50 faces (baked)
FEATURE [Part::FeaturePython] Screw1413  label="M3x35-Screw009"  # Fasteners workbench fastener (typed FeaturePython)
  Placement = pos=(-17.0542,-16.5,41.0035) rot=(1,0,0;1.5708rad)
  diameter = 1
  invert = true
  length = 9
  lengthCustom = 35
  matchOuter = true
  offset = 0
  thread = false
  type = 39
FEATURE [Part::Feature] Part__Feature112001169  label="mosquito_support001"
  Placement = pos=(-2.78e-14,-21.6,27.5) rot=(0,0,1;0rad)
  shape: bbox 40 x 20.25 x 12 mm, 97 faces (baked)
FEATURE [Part::FeaturePython] Screw1389  label="M3x8-Screw129"  # Fasteners workbench fastener (typed FeaturePython)
  Placement = pos=(3e-15,-20.15,-6) rot=(1,0,0;1.5708rad)
  baseObject = -> Part__Feature112001169 [Edge213]
  diameter = 4
  invert = true
  length = 10
  lengthCustom = 8
  matchOuter = true
  offset = 0
  thread = false
  type = 33
FEATURE [Part::Feature] Body001002002  label="endstop-cap001"
  Placement = pos=(16,7,54) rot=(1,0,0;3.14159rad)
  shape: bbox 12 x 13 x 7.75 mm, 19 faces (baked)
FEATURE [Part::FeaturePython] Screw1410  label="M2x10-self-tapping002"  # Fasteners workbench fastener (typed FeaturePython)
  Placement = pos=(22.75,10.25,53) rot=(0,0,1;0rad)
  baseObject = -> Body001002002 [Edge25]
  diameter = 2
  invert = false
  length = 5
  lengthCustom = 10
  matchOuter = true
  offset = 0
  thread = false
  type = 33
FEATURE [Part::FeaturePython] Screw1414  label="M2x10-self-tapping003"  # Fasteners workbench fastener (typed FeaturePython)
  Placement = pos=(22.75,3.75,53) rot=(0,0,1;0rad)
  baseObject = -> Body001002002 [Edge27]
  diameter = 2
  invert = false
  length = 5
  lengthCustom = 10
  matchOuter = true
  offset = 0
  thread = false
  type = 33
FEATURE [Part::FeaturePython] Screw1415  label="M3x40-Screw003"  # Fasteners workbench fastener (typed FeaturePython)
  Placement = pos=(18.5,25.5,19) rot=(0,1,0;1.5708rad)
  diameter = 4
  invert = false
  length = 10
  lengthCustom = 40
  matchOuter = true
  offset = 0
  thread = false
  type = 33
FEATURE [Part::FeaturePython] HeatSet035  label="M3x4-HeatSet028"  # WARN: FeaturePython — macro-defined, semantics opaque (R4)
  Placement = pos=(20,-36.5,11.7) rot=(0,1,0;1.5708rad)
  baseObject = -> Chamfer005021077002006007019003032007004003001009 [Edge128]
  diameter = 2
  invert = true
  offset = 0
FEATURE [Part::Feature] Body001002003  label="top-plate-with-endstop001"
  Placement = pos=(0,0,-44) rot=(0,0,1;3.14159rad)
  shape: bbox 50.05 x 27 x 13 mm, 100 faces (baked)
FEATURE [Part::FeaturePython] Nut066  label="M3-Nut039"  # Fasteners workbench fastener (typed FeaturePython)
  Placement = pos=(-17.5,8.59783,-20.5) rot=(1,0,0;1.5708rad)
  baseObject = -> Part__Feature112001181 [Edge75]
  diameter = 4
  invert = false
  matchOuter = true
  offset = 0
  thread = false
  type = 7
FEATURE [Part::Feature] Fusion036012039011002025018010027013001002002001002001029003  label="mosquito-hotend001"
  Placement = pos=(0,-31.5,-28) rot=(0,0,1;0rad)
  shape: bbox 27.01 x 18.86 x 47.01 mm, 355 faces, 0 solids (baked)
FEATURE [Part::FeaturePython] Nut067  label="M3-Nut040"  # Fasteners workbench fastener (typed FeaturePython)
  Placement = pos=(13,15.5,-7) rot=(-1,0,0;1.5708rad)
  diameter = 4
  invert = false
  matchOuter = true
  offset = 0
  thread = false
  type = 7
FEATURE [Part::Feature] Chamfer005021077002006007019003032007004003001008  label="extruder-cable-support001"
  Placement = pos=(0,29.5,32) rot=(1,0,0;1.5708rad)
  shape: bbox 38.86 x 11.83 x 29.43 mm, 90 faces (baked)
FEATURE [Part::FeaturePython] HeatSet036  label="M3x4-HeatSet029"  # WARN: FeaturePython — macro-defined, semantics opaque (R4)
  Placement = pos=(-7.5,2.5,51) rot=(0,0,1;0rad)
  baseObject = -> Fusion036012039011002025018010027013001002002001002001029004 [Edge5]
  diameter = 2
  invert = false
  offset = 0
FEATURE [Part::Feature] Part__Feature112001170  label="extruderbottom-plate001"
  Placement = pos=(0,17.6378,-29.79) rot=(1,0,0;1.5708rad)
  shape: bbox 44.1 x 27 x 22.2 mm, 66 faces (baked)
FEATURE [Part::Feature] Part__Feature112001171  label="adxl345 v057"
  shape: bbox 0.5 x 0.5 x 0.1 mm, 6 faces (baked)
FEATURE [Part::Feature] Part__Feature112001172  label="adxl345 v058"
  shape: bbox 0.5 x 0.5 x 0.1 mm, 6 faces (baked)
FEATURE [Part::FeaturePython] HeatSet037  label="M3x4-HeatSet030"  # WARN: FeaturePython — macro-defined, semantics opaque (R4)
  Placement = pos=(20,-36.5,3.7) rot=(0,1,0;1.5708rad)
  baseObject = -> Chamfer005021077002006007019003032007004003001009 [Edge127]
  diameter = 2
  invert = true
  offset = 0
FEATURE [Part::Feature] Part__Feature112001173  label="adxl345 v059"
  shape: bbox 4 x 2 x 1 mm, 6 faces (baked)
FEATURE [Part::Feature] Part__Feature112001174  label="adxl345 v060"
  shape: bbox 0.1911 x 0.3 x 0.1 mm, 6 faces (baked)
FEATURE [Part::Feature] Chamfer005021077002006007019003032007004003001009  label="dragon-mount-mod001"
  Placement = pos=(0,-31.5,33) rot=(0,0,1;0rad)
  shape: bbox 51.01 x 26.2 x 43.01 mm, 143 faces (baked)
FEATURE [Part::Feature] Part__Feature112001175  label="adxl345 v061"
  shape: bbox 0.2125 x 0.3 x 0.1 mm, 6 faces (baked)
FEATURE [Part::Feature] Part__Feature112001176  label="adxl345 v062"
  shape: bbox 0.2125 x 0.4 x 0.1 mm, 6 faces (baked)
FEATURE [Part::FeaturePython] Nut068  label="M3-Nut041"  # Fasteners workbench fastener (typed FeaturePython)
  Placement = pos=(-17.05,15.5,41) rot=(-1,0,0;1.5708rad)
  diameter = 4
  invert = false
  matchOuter = true
  offset = 0
  thread = false
  type = 7
FEATURE [Part::Feature] Part__Feature112001177  label="adxl345 v063"
  shape: bbox 0.5 x 0.5 x 0.15 mm, 6 faces (baked)
FEATURE [Part::Feature] Part__Feature112001178  label="4010-fan001"
  Placement = pos=(-2.4e-14,-43.5,14) rot=(0,0,1;0rad)
  shape: bbox 40 x 10 x 40 mm, 104 faces (baked)
FEATURE [Part::FeaturePython] Screw1390  label="M3x25-Screw031"  # Fasteners workbench fastener (typed FeaturePython)
  Placement = pos=(16,-55.5,-2) rot=(1,0,0;1.5708rad)
  baseObject = -> Part__Feature112001178 [Edge121]
  diameter = 4
  invert = false
  length = 10
  lengthCustom = 25
  matchOuter = true
  offset = 2
  thread = false
  type = 33
FEATURE [Part::FeaturePython] Screw1391  label="M3x25-Screw032"  # Fasteners workbench fastener (typed FeaturePython)
  Placement = pos=(-16,-55.5,-2) rot=(1,0,0;1.5708rad)
  baseObject = -> Part__Feature112001178 [Edge127]
  diameter = 4
  invert = false
  length = 10
  lengthCustom = 25
  matchOuter = true
  offset = 2
  thread = false
  type = 33
FEATURE [Part::FeaturePython] Screw1392  label="M3x20-Screw025"  # Fasteners workbench fastener (typed FeaturePython)
  Placement = pos=(-16,-55.5,30) rot=(1,0,0;1.5708rad)
  baseObject = -> Part__Feature112001178 [Edge130]
  diameter = 4
  invert = false
  length = 10
  lengthCustom = 20
  matchOuter = true
  offset = 2
  thread = false
  type = 33
FEATURE [Part::FeaturePython] Screw1405  label="M3x20-Screw026"  # Fasteners workbench fastener (typed FeaturePython)
  Placement = pos=(16,-55.5,30) rot=(1,0,0;1.5708rad)
  baseObject = -> Part__Feature112001178 [Edge124]
  diameter = 4
  invert = false
  length = 10
  lengthCustom = 20
  matchOuter = true
  offset = 2
  thread = false
  type = 33
FEATURE [Part::Feature] Part__Feature112001179  label="adxl345 v064"
  shape: bbox 0.5 x 0.5 x 0.1 mm, 6 faces (baked)
FEATURE [Part::Feature] Part__Feature112001180  label="adxl345 v065"
  shape: bbox 0.1911 x 0.4 x 0.1 mm, 6 faces (baked)
FEATURE [Part::Feature] Part__Feature112001181  label="duct-tri-horn001"
  Placement = pos=(0,10.5978,-18) rot=(1,0,0;1.5708rad)
  shape: bbox 65.34 x 50.74 x 15.61 mm, 106 faces (baked)
FEATURE [Part::FeaturePython] Screw1417  label="M3x8-Screw130"  # Fasteners workbench fastener (typed FeaturePython)
  Placement = pos=(0,7.5,48.5) rot=(0,0,1;0rad)
  diameter = 1
  invert = false
  length = 1
  lengthCustom = 8
  matchOuter = true
  offset = 0
  thread = false
  type = 39
FEATURE [Part::Feature] Fusion036012039011002025018010027013001002002001002001029004  label="adxl-mount001"
  Placement = pos=(0,-31.5,33) rot=(0,0,1;0rad)
  shape: bbox 22 x 12.5 x 6.5 mm, 26 faces (baked)
FEATURE [Part::FeaturePython] Screw1407  label="M3x6-Screw106"  # Fasteners workbench fastener (typed FeaturePython)
  Placement = pos=(-7.5,2.5,53) rot=(0,0,1;0rad)
  baseObject = -> Fusion036012039011002025018010027013001002002001002001029004 [Edge2]
  diameter = 4
  invert = false
  length = 1
  lengthCustom = 6
  matchOuter = true
  offset = 2.4
  thread = false
  type = 33
FEATURE [Part::FeaturePython] Screw1416  label="M3x6-Screw107"  # Fasteners workbench fastener (typed FeaturePython)
  Placement = pos=(7.5,2.5,52.6) rot=(0,0,1;0rad)
  baseObject = -> Fusion036012039011002025018010027013001002002001002001029004 [Edge47]
  diameter = 4
  invert = false
  length = 1
  lengthCustom = 6
  matchOuter = true
  offset = 2
  thread = false
  type = 33
FEATURE [Part::Feature] Part__Feature112001182  label="adxl345 v066"
  shape: bbox 6 x 3 x 0.5 mm, 6 faces (baked)
FEATURE [App::Part] adxl345_v004  label="adxl346"
  Group = -> [Part__Feature112001182,Part__Feature112001160,Part__Feature112001173,Part__Feature112001175,Part__Feature112001171,Part__Feature112001159,Part__Feature112001145,Part__Feature112001167,Part__Feature112001144,Part__Feature112001150,Part__Feature112001156,Part__Feature112001163,Part__Feature112001176,Part__Feature112001147,Part__Feature112001148,Part__Feature112001152,Part__Feature112001172,+15 more]
  Origin = -> Origin207
  Placement = pos=(-10,0.5,52.5) rot=(0,0,1;0rad)
FEATURE [App::Part] Part198  label="toolhead-carrier-sherpa-1516"
  Group = -> [Fusion036012039011002025018010027013001002002001002001029003,Part__Feature112001169,Part__Feature112001153,Part__Feature112001178,BL_Touch__1_002,Nut063,Nut064,Nut062,Nut067,Screw1387,Screw1415,Nut068,Screw1404,Screw1412,Screw1398,Screw1409,Screw1401,Screw1395,Screw1397,Screw1406,Screw1408,Screw1389,Screw1388,Screw1400,Screw1411,Screw1396,Screw1405,Screw1390,Screw1391,Screw1392,adxl345_v004,+42 more]
  Origin = -> Origin209
  Placement = pos=(135,7.5,-5) rot=(0,0,1;0rad)
